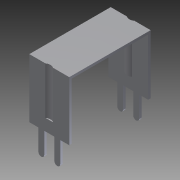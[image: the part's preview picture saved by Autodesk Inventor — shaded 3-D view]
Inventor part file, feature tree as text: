
AUTODESK INVENTOR PART (.ipt)
format: ipt  version: 2014 (Build 180170000, 170)  size: 129,536 bytes
history: native  units: in
note: dims shown in document units (in); Inventor stores cm internally (conversion verified against a paired STEP export)
features: other x7, extrude x6, sketch x6
ambient origin geometry x8: Origin, YZ Plane, XZ Plane, XY Plane, X Axis, Y Axis, Z Axis, Center Point
bodies: Solid1 (feature_tree)
feature tree (19):
  extrude  "Extrusion1"  Depth=0.642in TaperAngle=0.0deg
  extrude  "Extrusion2"  Depth=0.372in TaperAngle=0.0deg
  extrude  "Extrusion3"  Depth=0.372in TaperAngle=0.0deg
  extrude  "Extrusion4"  [1 undecoded]
  extrude  "Extrusion5"  [1 undecoded]
  extrude  "Extrusion6"  [1 undecoded]
  other  "bracket_to_switch_XY"
  other  "bracket_to_switch_YZ"
  other  "bracket_to_switch_ZX"
  other  "bracket_to_switch_X"
  other  "bracket_to_switch_Y"
  other  "bracket_to_switch_Z"
  other  "bracket_to_switch_Center"
  sketch  "Sketch_1"  dims[d0=0.315in d1=0.0in d2=0.642in d3=0.0in]
  sketch  "Sketch_2"  dims[d4=0.372in d5=0.0in d6=0.372in d7=0.0in]
  sketch  "Sketch_3"  dims[d8=0.372in d9=0.0in d10=0.372in d11=0.0in]
  sketch  "Sketch_4"
  sketch  "Sketch_5"
  sketch  "Sketch_6"
note: 3 required parameter values undecoded (feature->parameter linkage not recoverable at this tier; creation-order binding heuristic only, values carry confidence <= 0.55)
